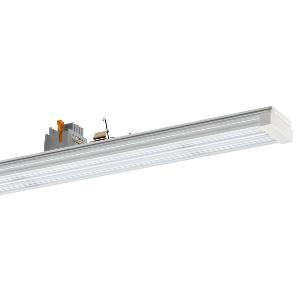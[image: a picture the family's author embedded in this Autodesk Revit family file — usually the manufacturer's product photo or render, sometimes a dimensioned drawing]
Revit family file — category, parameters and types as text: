
# Revit family: conveo_-_cvg_15000_850_w-p_da_7_226848069-00804942_92d9
name_source: partatom
category: Lighting Fixtures
units: mm (PartAtom-declared; Revit-internal decimal feet)

## family parameters
Cut with Voids When Loaded = No
Host = Face
Light Source = No
Part Type = Normal
Room Calculation Point = No
Round Connector Dimension = Use Diameter
Shared = No

## types (1)
- CONVEO - CVG 15000/850/W-P/DA/7 (1 x LED, 15100 lm, 5000K)
    Apparent Load = 100 VA
    Approval mark = CE
    CIE Flux Codes = 54 85 97 100 100
    Color Rendering = 80-89
    Color Temperature = 5000K
    Control Gear = Electronic ballast
    Default Elevation = 1800 mm
    Description = CVG 15000/850/W-P/DA/7|Continuous-row system|light source: LED|work equipment: Adjustable electronic ballast, digital DALI|connected load: 220-240 V, 50-60 Hz|Power consumption: approx. 100 W|luminous flux: 15100 lm|luminous efficacy: 151 lm/W|colour temperature: Cold white, ca. 5000 K|color rendering index (CRI): >= 80|chromaticity tolerance:  3 SDCM|System of protection: IP 54|class of protection: I|technology: Continuously dimmable|luminaire body|material: Aluminium|surface: Powder coatet|colour: White|lamp cover: Acrylic (PMMA), Satine|weight (net): approx. 2.2 kg|Fastening: Available separately|minimum ambient temperature: -25 ░C|maximum ambient temperature: 33 ░C|glare control: Prism optics (linear)|Approval mark: VDE - ENEC|
    Frequency = 50 Hz
    Height = 70 mm
    Lamp = 1 x LED
    Lamp Light Flux = 15100 lm
    Lamp count = 1
    Length = 1500 mm
    Luminous efficacy = 151 lm/W
    Manufacturer = Waldmann
    ModVariant = No
    Model = 226848069-00804942
    Mounting Place = Ceiling
    Mounting Type = Pendant
    Number of Poles = 1
    OnlyDefault = Yes
    Power Factor = 1
    Product Name = CONVEO - CVG 15000/850/W-P/DA/7
    Product group = Continuous-row system (industry)
    ProductGroupID = 301
    Protection Class = Protection class I
    Protection Degree = IP 54
    RLX_Detail_Level = 1
    RlxData = <blob elided: 132705 chars, md5=b0cd5717>
    Socket = socket
    Standby Power = 0 W
    System Light Flux = 15100 lm
    System Power = 100 W
    Type Comments = Product without accessories
    Type Image = 226848059-00804941-2p7.jpg
    URL = http://relux.com
    VarID = ---
    Voltage = 230 V
    Voltage Range = 220-240 V
    Weight = 0.00 kg
    Width = 64 mm

## geometry (parser evidence)
native form markers: Blend x4, Sweep x7
no freeform markers — native parametric forms only
